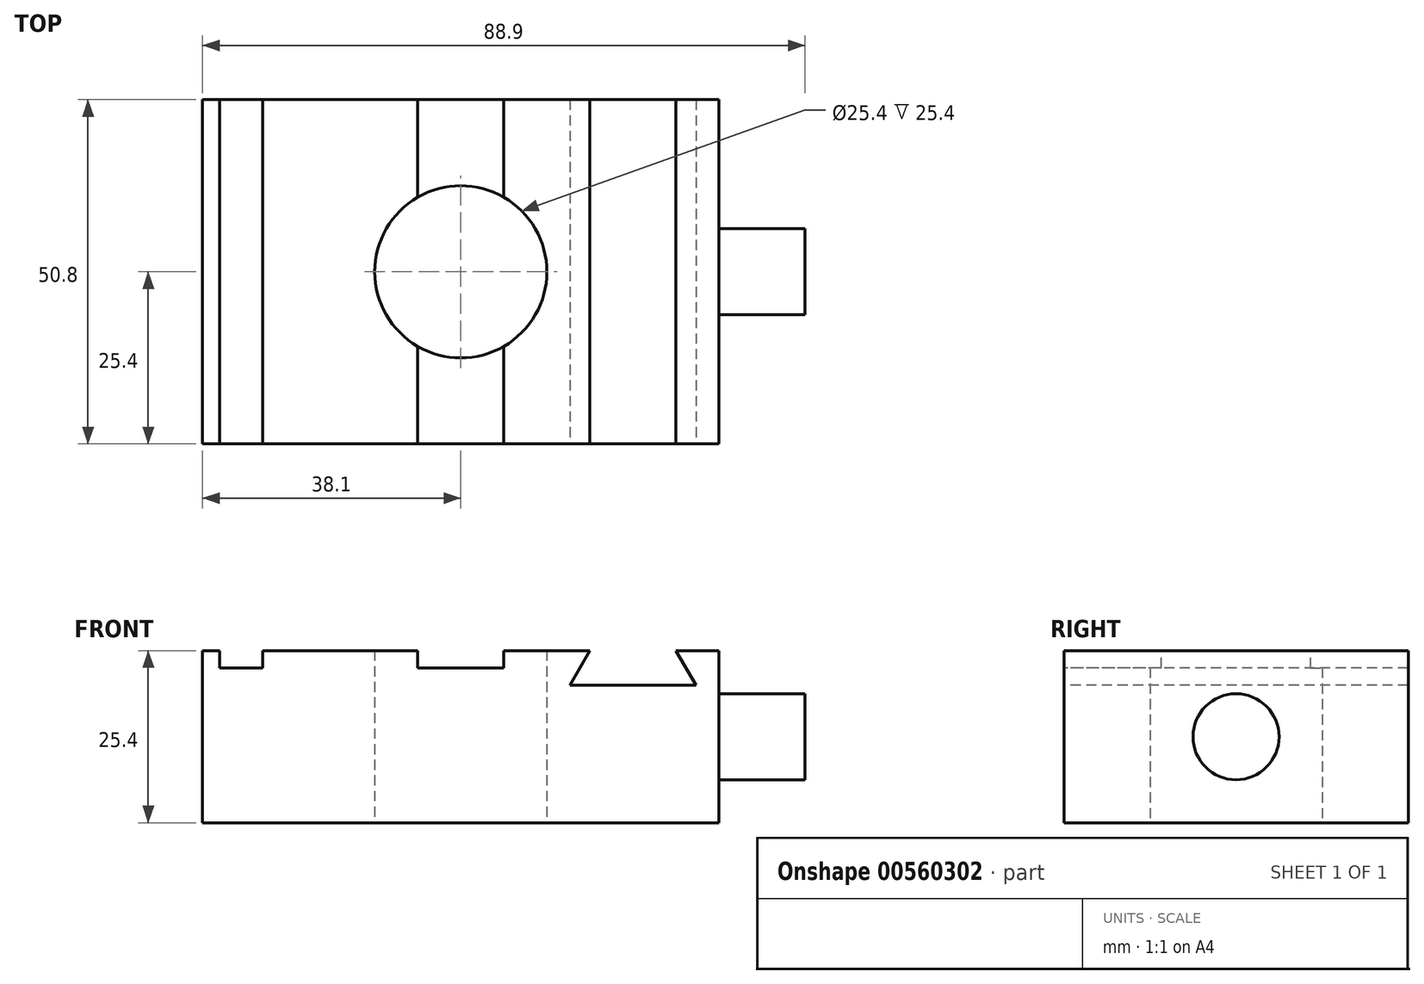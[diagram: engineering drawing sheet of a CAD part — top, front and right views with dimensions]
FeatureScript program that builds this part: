
annotation { "Feature Type Name" : "Feature", "Feature Type Description" : "" }
export const myFeature = defineFeature(function(context is Context, id is Id, definition is map)
    precondition{}
    {
        {
            var Q0;
            Q0=qCreatedBy(makeId("Top.planeOp"),FACE);
            var sketch = newSketch(context, id + "F0", { "sketchPlane" : qUnion([Q0])});
            skLineSegment(sketch, "E0.bottom", {"start": v(38.1, -25.4) * mm, "end": v(-38.1, -25.4) * mm});
            skLineSegment(sketch, "E0.top", {"start": v(38.1, 25.4) * mm, "end": v(-38.1, 25.4) * mm});
            skLineSegment(sketch, "E0.left", {"start": v(38.1, -25.4) * mm, "end": v(38.1, 25.4) * mm});
            skLineSegment(sketch, "E0.right", {"start": v(-38.1, -25.4) * mm, "end": v(-38.1, 25.4) * mm});
            skPoint(sketch, "E0.middle", {"position": v(0, 0) * mm});
            skCircle(sketch, "E1", {"center": v(0, 0) * mm, "radius": 12.7 * mm});
            skSolve(sketch);
        }
        {
            var Q0;
            Q0=makeQuery(id+"F0.imprint","IMPRINT",FACE,{"disambiguationData":[TD([[makeQuery(id+"F0.imprint","IMPRINT",EDGE,{"derivedFrom":sQuery(id+"F0.wireOp",EDGE,"E0.bottom")}),-1.0]])]});
            extrude(context, id + "F1", {"entities" : qUnion([Q0]), "depth" : 25.4 * mm, "offsetDistance" : 25 * mm});
        }
        {
            var Q0;
            Q0=makeQuery(id+"F1.opExtrude","CAP_FACE",FACE,{"disambiguationData":[OSD([sQuery(id+"F0.wireOp",EDGE,"E0.bottom"),sQuery(id+"F0.wireOp",EDGE,"E0.top"),sQuery(id+"F0.wireOp",EDGE,"E0.left"),sQuery(id+"F0.wireOp",EDGE,"E0.right"),sQuery(id+"F0.wireOp",EDGE,"E1")])],"isStart":false});
            var sketch = newSketch(context, id + "F2", { "sketchPlane" : qUnion([Q0])});
            skLineSegment(sketch, "E2.bottom", {"start": v(-35.56, 25.4) * mm, "end": v(-29.21, 25.4) * mm});
            skLineSegment(sketch, "E2.top", {"start": v(-35.56, -25.4) * mm, "end": v(-29.21, -25.4) * mm});
            skLineSegment(sketch, "E2.left", {"start": v(-35.56, 25.4) * mm, "end": v(-35.56, -25.4) * mm});
            skLineSegment(sketch, "E2.right", {"start": v(-29.21, 25.4) * mm, "end": v(-29.21, -25.4) * mm});
            skLineSegment(sketch, "E3", {"start": v(-6.35, 25.4) * mm, "end": v(-6.35, -25.4) * mm});
            skLineSegment(sketch, "E4", {"start": v(-6.35, -25.4) * mm, "end": v(6.35, -25.4) * mm});
            skLineSegment(sketch, "E5", {"start": v(6.35, -25.4) * mm, "end": v(6.35, 25.4) * mm});
            skLineSegment(sketch, "E6", {"start": v(6.35, 25.4) * mm, "end": v(-6.35, 25.4) * mm});
            skLineSegment(sketch, "E7", {"start": v(0, 25.4) * mm, "end": v(0, -25.4) * mm, "construction": true});
            skSolve(sketch);
        }
        {
            var Q0;
            Q0=makeQuery(id+"F2.imprint","IMPRINT",FACE,{"disambiguationData":[TD([[makeQuery(id+"F2.imprint","IMPRINT",EDGE,{"derivedFrom":sQuery(id+"F2.wireOp",EDGE,"E2.bottom")}),1.0]])]});
            var Q1;
            {var subQ0=sQuery(id+"F2.wireOp",EDGE,"E6");Q1=makeQuery(id+"F2.imprint","IMPRINT",FACE,{"disambiguationData":[TD([[makeQuery(id+"F2.imprint","IMPRINT",EDGE,{"derivedFrom":subQ0}),1.0]])]});}
            var Q2;
            {var subQ0=sQuery(id+"F2.wireOp",EDGE,"E4");Q2=makeQuery(id+"F2.imprint","IMPRINT",FACE,{"disambiguationData":[TD([[makeQuery(id+"F2.imprint","IMPRINT",EDGE,{"derivedFrom":subQ0}),-1.0]])]});}
            extrude(context, id + "F3", {"entities" : qUnion([Q0, Q1, Q2]), "operationType" : NewBodyOperationType.REMOVE, "oppositeDirection" : true, "depth" : 2.54 * mm, "offsetDistance" : 25 * mm});
        }
        {
            var Q0;
            Q0=makeQuery(id+"F1.opExtrude","SWEPT_FACE",FACE,{"disambiguationData":[OSD([sQuery(id+"F0.wireOp",EDGE,"E0.bottom")])]});
            var sketch = newSketch(context, id + "F4", { "sketchPlane" : qUnion([Q0])});
            skLineSegment(sketch, "E8", {"start": v(19.05, 25.4) * mm, "end": v(16.12, 20.32) * mm});
            skLineSegment(sketch, "E9", {"start": v(16.12, 20.32) * mm, "end": v(34.68, 20.32) * mm});
            skLineSegment(sketch, "E10", {"start": v(34.68, 20.32) * mm, "end": v(31.75, 25.4) * mm});
            skLineSegment(sketch, "E11", {"start": v(31.75, 25.4) * mm, "end": v(19.05, 25.4) * mm});
            skLineSegment(sketch, "E12", {"start": v(25.4, 25.4) * mm, "end": v(25.4, 20.32) * mm, "construction": true});
            skSolve(sketch);
        }
        {
            var Q0;
            Q0 = qSketchRegion(id + "F4", true);
            extrude(context, id + "F5", {"entities" : qUnion([Q0]), "operationType" : NewBodyOperationType.REMOVE, "endBound" : BoundingType.THROUGH_ALL, "oppositeDirection" : true, "depth" : 25.4 * mm, "offsetDistance" : 25.4 * mm});
        }
        {
            var Q0;
            Q0=makeQuery(id+"F1.opExtrude","SWEPT_FACE",FACE,{"disambiguationData":[OSD([sQuery(id+"F0.wireOp",EDGE,"E0.left")])]});
            var sketch = newSketch(context, id + "F6", { "sketchPlane" : qUnion([Q0])});
            skCircle(sketch, "E13", {"center": v(0, 12.7) * mm, "radius": 6.35 * mm});
            skPoint(sketch, "E13.centerSnap0", {"position": v(-25.4, 12.7) * mm});
            skPoint(sketch, "E13.centerSnap1", {"position": v(0, 25.4) * mm});
            skSolve(sketch);
        }
        {
            var Q0;
            Q0=makeQuery(id+"F6.imprint","IMPRINT",FACE,{"disambiguationData":[TD([[makeQuery(id+"F6.imprint","IMPRINT",EDGE,{"derivedFrom":sQuery(id+"F6.wireOp",EDGE,"E13")}),1.0]])]});
            extrude(context, id + "F7", {"entities" : qUnion([Q0]), "depth" : 12.7 * mm, "offsetDistance" : 25.4 * mm});
        }
    });
